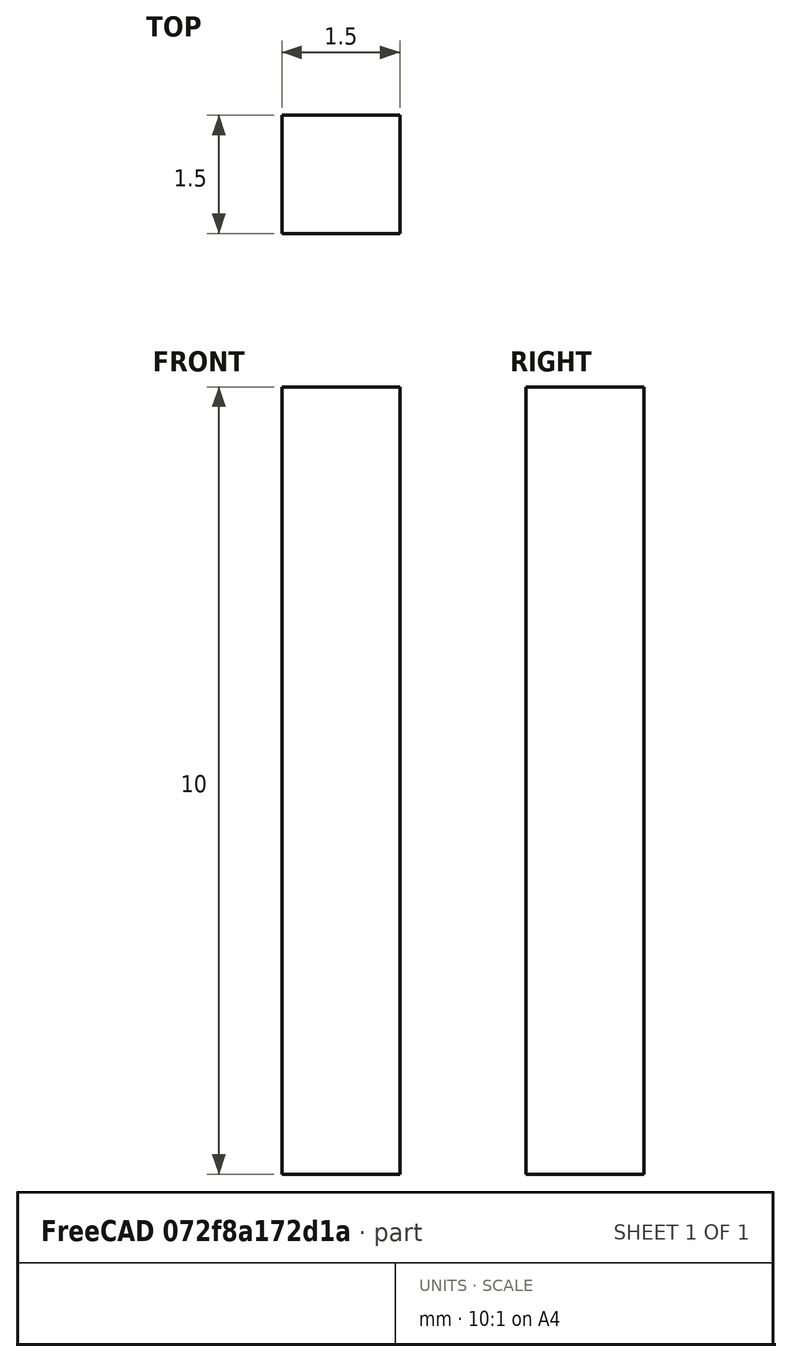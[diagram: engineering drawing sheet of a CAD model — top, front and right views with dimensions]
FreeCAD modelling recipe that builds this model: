
FCSTD DOCUMENT  (FreeCAD 0.16R6712 (Git))
Label: qwerrewwee
License: All rights reserved
LicenseURL: http://en.wikipedia.org/wiki/All_rights_reserved
objects: Sketcher::SketchObject×5, PartDesign::Pad×1
note: 7 computed .brp shape members not serialized (recipe doc carries the construction recipe); baked Part::Feature solids carry a one-line shape summary decoded from their .brp

FEATURE [Sketcher::SketchObject] Sketch
FEATURE [Sketcher::SketchObject] Sketch001
FEATURE [Sketcher::SketchObject] Sketch002
  sketch-geometry (4):
    g0: LineSegment StartX=-0.75 StartY=-0.75 StartZ=0 EndX=0.75 EndY=-0.75 EndZ=0
    g1: LineSegment StartX=0.75 StartY=-0.75 StartZ=0 EndX=0.75 EndY=0.75 EndZ=0
    g2: LineSegment StartX=0.75 StartY=0.75 StartZ=0 EndX=-0.75 EndY=0.75 EndZ=0
    g3: LineSegment StartX=-0.75 StartY=0.75 StartZ=0 EndX=-0.75 EndY=-0.75 EndZ=0
  constraints (13):
    c: Coincident(g0,g1)
    c: Coincident(g1,g2)
    c: Coincident(g2,g3)
    c: Coincident(g3,g0)
    c: Horizontal(g0)
    c: Horizontal(g2)
    c: Vertical(g1)
    c: Vertical(g3)
    c: Symmetric(g2,g0,g-1)
    c: Symmetric(g1,g0,g-1)
    c: DistanceX(g2,g2) = 1.5
    c: DistanceY(g1,g1) = 1.5
    c: Symmetric(g2,g1,g-2)
FEATURE [Sketcher::SketchObject] Sketch003
FEATURE [Sketcher::SketchObject] Sketch004
FEATURE [PartDesign::Pad] Pad
  Length = 10
  Length2 = 100
  Sketch = -> Sketch002
  Type = 0
